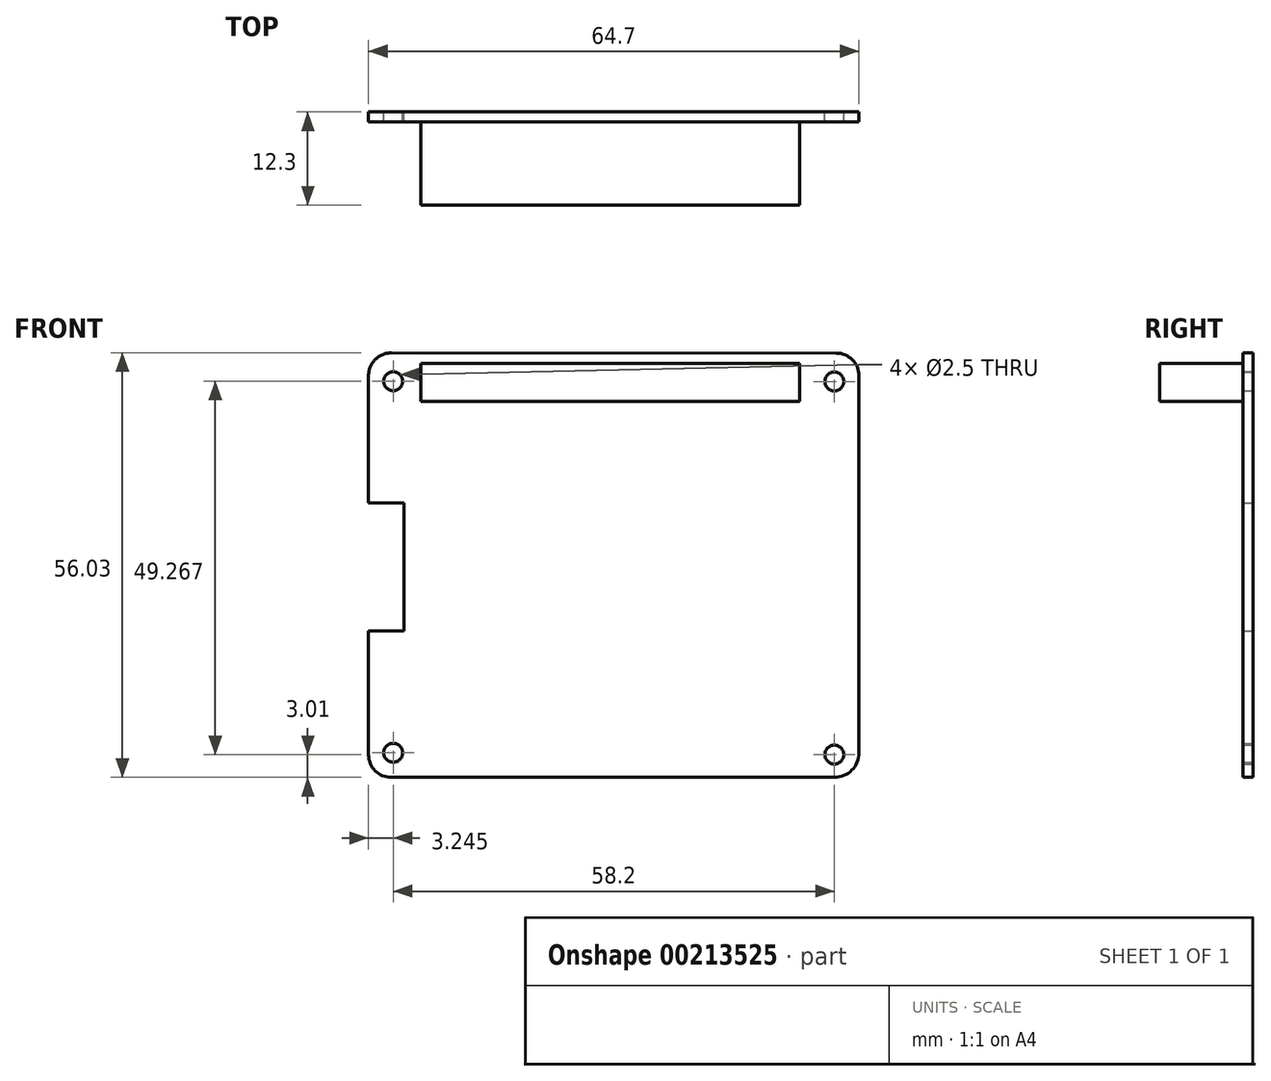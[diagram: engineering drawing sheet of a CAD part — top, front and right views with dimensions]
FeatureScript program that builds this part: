
annotation { "Feature Type Name" : "Feature", "Feature Type Description" : "" }
export const myFeature = defineFeature(function(context is Context, id is Id, definition is map)
    precondition{}
    {
        {
            var Q0;
            Q0=qCreatedBy(makeId("Front.planeOp"),FACE);
            var sketch = newSketch(context, id + "F0", { "sketchPlane" : qUnion([Q0])});
            skLineSegment(sketch, "E0", {"start": v(31.55, 21.56) * mm, "end": v(31.55, -28.2) * mm});
            skLineSegment(sketch, "E1", {"start": v(28.3, -31.44) * mm, "end": v(-30.15, -31.44) * mm});
            skLineSegment(sketch, "E2", {"start": v(-33.15, -28.44) * mm, "end": v(-33.15, -12.14) * mm});
            skLineSegment(sketch, "E3", {"start": v(-33.15, -12.14) * mm, "end": v(-28.45, -12.14) * mm});
            skLineSegment(sketch, "E4", {"start": v(-28.45, -12.14) * mm, "end": v(-28.45, 4.76) * mm});
            skLineSegment(sketch, "E5", {"start": v(-28.45, 4.76) * mm, "end": v(-33.15, 4.76) * mm});
            skLineSegment(sketch, "E6", {"start": v(-33.15, 4.76) * mm, "end": v(-33.15, 21.59) * mm});
            skLineSegment(sketch, "E7", {"start": v(28.55, 24.56) * mm, "end": v(-30.15, 24.59) * mm});
            skLineSegment(sketch, "E8", {"start": v(31.55, 24.56) * mm, "end": v(31.55, 20.8) * mm, "construction": true});
            skPoint(sketch, "E9.visualSharp", {"position": v(-33.15, 24.59) * mm});
            skArc(sketch, "E9.filletArc", {"start": v(-30.15, 24.59) * mm, "mid": v(-32.28, 23.7) * mm, "end": v(-33.15, 21.59) * mm});
            skPoint(sketch, "E10.visualSharp", {"position": v(-33.15, -31.44) * mm});
            skArc(sketch, "E10.filletArc", {"start": v(-33.15, -28.44) * mm, "mid": v(-32.28, -30.56) * mm, "end": v(-30.15, -31.44) * mm});
            skPoint(sketch, "E11.visualSharp", {"position": v(31.55, -31.44) * mm});
            skArc(sketch, "E11.filletArc", {"start": v(28.3, -31.44) * mm, "mid": v(30.6, -30.5) * mm, "end": v(31.55, -28.2) * mm});
            skPoint(sketch, "E12.visualSharp", {"position": v(31.55, 24.56) * mm});
            skArc(sketch, "E12.filletArc", {"start": v(31.55, 21.56) * mm, "mid": v(30.67, 23.68) * mm, "end": v(28.55, 24.56) * mm});
            skLineSegment(sketch, "E13", {"start": v(31.55, 20.8) * mm, "end": v(28.3, 20.8) * mm});
            skCircle(sketch, "E14", {"center": v(28.3, 20.8) * mm, "radius": 1.25 * mm});
            skLineSegment(sketch, "E15", {"start": v(31.55, -31.44) * mm, "end": v(31.55, -28.2) * mm, "construction": true});
            skLineSegment(sketch, "E16", {"start": v(28.3, 20.8) * mm, "end": v(28.3, -45.28) * mm, "construction": true});
            skLineSegment(sketch, "E17", {"start": v(31.55, -28.2) * mm, "end": v(28.3, -28.2) * mm, "construction": true});
            skLineSegment(sketch, "E18", {"start": v(-33.15, -31.44) * mm, "end": v(-29.9, -31.44) * mm, "construction": true});
            skLineSegment(sketch, "E19", {"start": v(-22.27, 24.58) * mm, "end": v(-22.27, 18.18) * mm, "construction": true});
            skLineSegment(sketch, "E20", {"start": v(-33.15, 18.18) * mm, "end": v(-26.25, 18.18) * mm, "construction": true});
            skLineSegment(sketch, "E21", {"start": v(-26.25, 18.18) * mm, "end": v(-26.25, 23.18) * mm});
            skLineSegment(sketch, "E22", {"start": v(-26.25, 18.18) * mm, "end": v(23.75, 18.18) * mm});
            skLineSegment(sketch, "E23", {"start": v(23.75, 18.18) * mm, "end": v(23.75, 23.18) * mm});
            skLineSegment(sketch, "E24", {"start": v(-26.25, 23.18) * mm, "end": v(23.75, 23.18) * mm});
            skCircle(sketch, "E25", {"center": v(28.3, -28.43) * mm, "radius": 1.25 * mm});
            skCircle(sketch, "E26", {"center": v(-29.9, -28.2) * mm, "radius": 1.25 * mm});
            skLineSegment(sketch, "E27", {"start": v(-30.15, 24.59) * mm, "end": v(-30.15, 20.84) * mm, "construction": true});
            skLineSegment(sketch, "E28", {"start": v(-29.9, -31.44) * mm, "end": v(-29.9, 27.6) * mm, "construction": true});
            skLineSegment(sketch, "E29", {"start": v(-30.15, 20.84) * mm, "end": v(-29.27, 20.84) * mm, "construction": true});
            skCircle(sketch, "E30", {"center": v(-29.9, 20.84) * mm, "radius": 1.25 * mm});
            skSolve(sketch);
        }
        {
            var Q0;
            Q0=makeQuery(id+"F0.imprint","IMPRINT",FACE,{"disambiguationData":[TD([[makeQuery(id+"F0.imprint","IMPRINT",EDGE,{"derivedFrom":sQuery(id+"F0.wireOp",EDGE,"E1")}),-1.0]])]});
            extrude(context, id + "F1", {"entities" : qUnion([Q0]), "depth" : 1.3 * mm});
        }
        {
            var Q0;
            Q0=makeQuery(id+"F0.imprint","IMPRINT",FACE,{"disambiguationData":[TD([[makeQuery(id+"F0.imprint","IMPRINT",EDGE,{"derivedFrom":sQuery(id+"F0.wireOp",EDGE,"E21")}),-1.0]])]});
            extrude(context, id + "F2", {"entities" : qUnion([Q0]), "operationType" : NewBodyOperationType.ADD, "depth" : 12.3 * mm});
        }
    });
